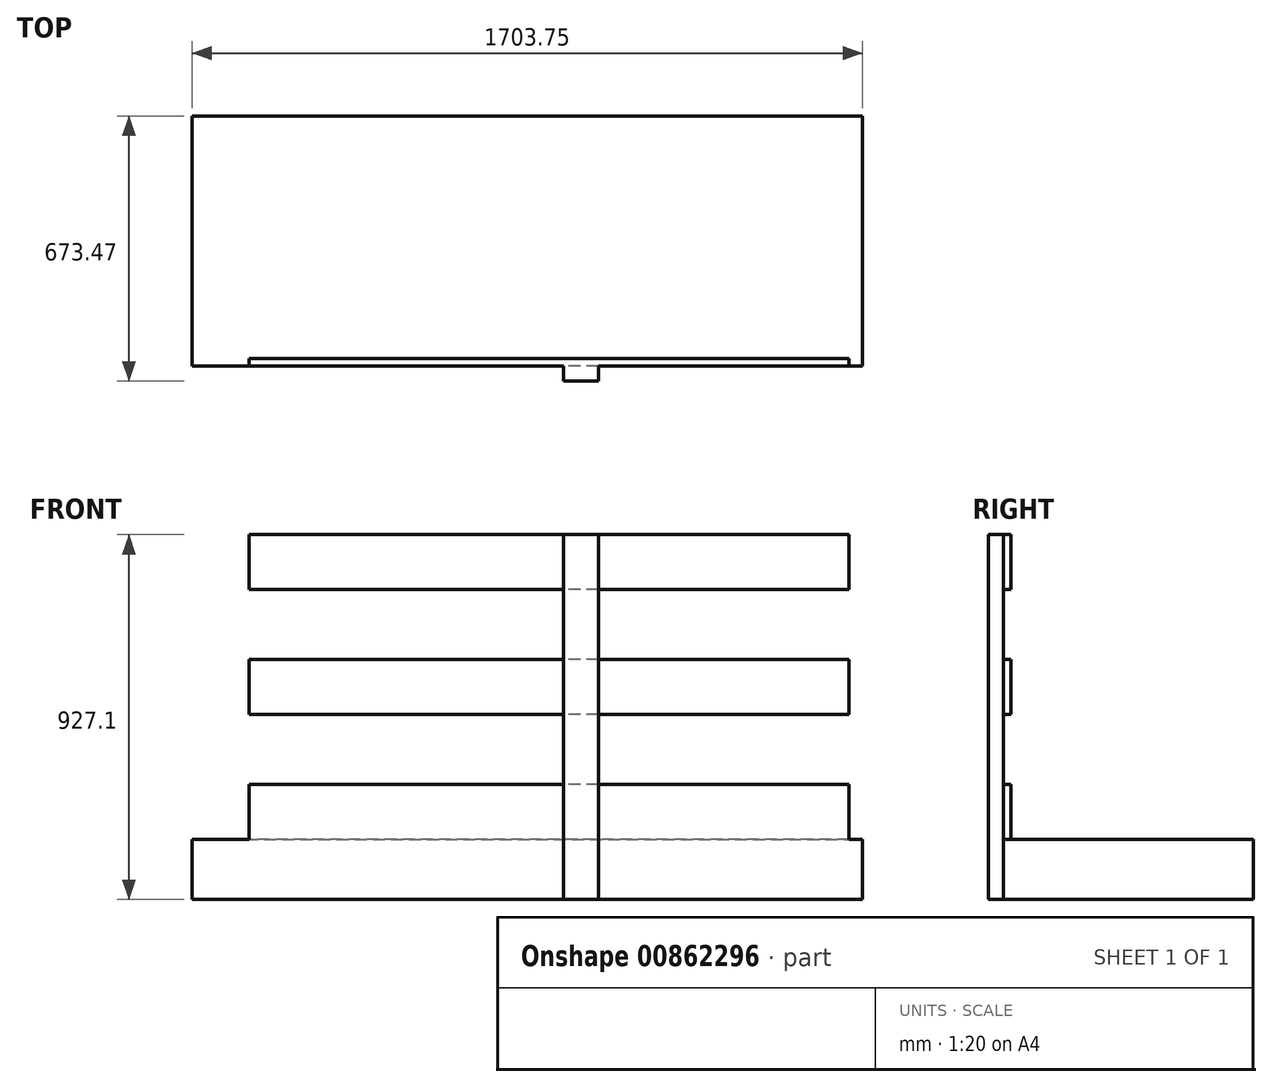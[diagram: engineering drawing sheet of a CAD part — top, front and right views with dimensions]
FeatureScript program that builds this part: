
annotation { "Feature Type Name" : "Feature", "Feature Type Description" : "" }
export const myFeature = defineFeature(function(context is Context, id is Id, definition is map)
    precondition{}
    {
        {
            var Q0;
            Q0=qCreatedBy(makeId("Front.planeOp"),FACE);
            var sketch = newSketch(context, id + "F0", { "sketchPlane" : qUnion([Q0])});
            skLineSegment(sketch, "E0.bottom", {"start": v(0, 0) * mm, "end": v(88.9, 0) * mm});
            skLineSegment(sketch, "E0.top", {"start": v(0, 927.1) * mm, "end": v(88.9, 927.1) * mm});
            skLineSegment(sketch, "E0.left", {"start": v(0, 0) * mm, "end": v(0, 927.1) * mm});
            skLineSegment(sketch, "E0.right", {"start": v(88.9, 0) * mm, "end": v(88.9, 927.1) * mm});
            skSolve(sketch);
        }
        {
            var Q0;
            Q0=makeQuery(id+"F0.imprint","IMPRINT",FACE,{"disambiguationData":[TD([[makeQuery(id+"F0.imprint","IMPRINT",EDGE,{"derivedFrom":sQuery(id+"F0.wireOp",EDGE,"E0.bottom")}),1.0]])]});
            extrude(context, id + "F1", {"entities" : qUnion([Q0]), "depth" : 38.1 * mm, "offsetDistance" : 25.4 * mm});
        }
        {
            var Q0;
            Q0=makeQuery(id+"F1.opExtrude","CAP_FACE",FACE,{"disambiguationData":[OSD([sQuery(id+"F0.wireOp",EDGE,"E0.bottom"),sQuery(id+"F0.wireOp",EDGE,"E0.top"),sQuery(id+"F0.wireOp",EDGE,"E0.left"),sQuery(id+"F0.wireOp",EDGE,"E0.right")])],"isStart":true});
            var sketch = newSketch(context, id + "F2", { "sketchPlane" : qUnion([Q0])});
            skLineSegment(sketch, "E1.bottom", {"start": v(-725.49, 292.1) * mm, "end": v(798.51, 292.1) * mm});
            skLineSegment(sketch, "E1.top", {"start": v(-725.49, 152.4) * mm, "end": v(798.51, 152.4) * mm});
            skLineSegment(sketch, "E1.left", {"start": v(-725.49, 292.1) * mm, "end": v(-725.49, 152.4) * mm});
            skLineSegment(sketch, "E1.right", {"start": v(798.51, 292.1) * mm, "end": v(798.51, 152.4) * mm});
            skLineSegment(sketch, "E2.bottom", {"start": v(-725.49, 469.9) * mm, "end": v(798.51, 469.9) * mm});
            skLineSegment(sketch, "E2.top", {"start": v(-725.49, 609.6) * mm, "end": v(798.51, 609.6) * mm});
            skLineSegment(sketch, "E2.left", {"start": v(-725.49, 469.9) * mm, "end": v(-725.49, 609.6) * mm});
            skLineSegment(sketch, "E2.right", {"start": v(798.51, 469.9) * mm, "end": v(798.51, 609.6) * mm});
            skLineSegment(sketch, "E3.bottom", {"start": v(-725.49, 787.4) * mm, "end": v(798.51, 787.4) * mm});
            skLineSegment(sketch, "E3.top", {"start": v(-725.49, 927.1) * mm, "end": v(798.51, 927.1) * mm});
            skLineSegment(sketch, "E3.left", {"start": v(-725.49, 787.4) * mm, "end": v(-725.49, 927.1) * mm});
            skLineSegment(sketch, "E3.right", {"start": v(798.51, 787.4) * mm, "end": v(798.51, 927.1) * mm});
            skSolve(sketch);
        }
        {
            var Q0;
            Q0 = qSketchRegion(id + "F2", true);
            extrude(context, id + "F3", {"entities" : qUnion([Q0]), "operationType" : NewBodyOperationType.ADD, "depth" : 19.05 * mm, "offsetDistance" : 25.4 * mm});
        }
        {
            var Q0;
            Q0=qCreatedBy(makeId("Top.planeOp"),FACE);
            var sketch = newSketch(context, id + "F4", { "sketchPlane" : qUnion([Q0])});
            skLineSegment(sketch, "E4.bottom", {"start": v(-944.08, 635.37) * mm, "end": v(759.67, 635.37) * mm});
            skLineSegment(sketch, "E4.top", {"start": v(-944.08, 0) * mm, "end": v(759.67, 0) * mm});
            skLineSegment(sketch, "E4.left", {"start": v(-944.08, 635.37) * mm, "end": v(-944.08, 0) * mm});
            skLineSegment(sketch, "E4.right", {"start": v(759.67, 635.37) * mm, "end": v(759.67, 0) * mm});
            skSolve(sketch);
        }
        {
            var Q0;
            Q0 = qSketchRegion(id + "F4", true);
            extrude(context, id + "F5", {"entities" : qUnion([Q0]), "operationType" : NewBodyOperationType.ADD, "depth" : 152.4 * mm, "offsetDistance" : 25.4 * mm});
        }
    });
